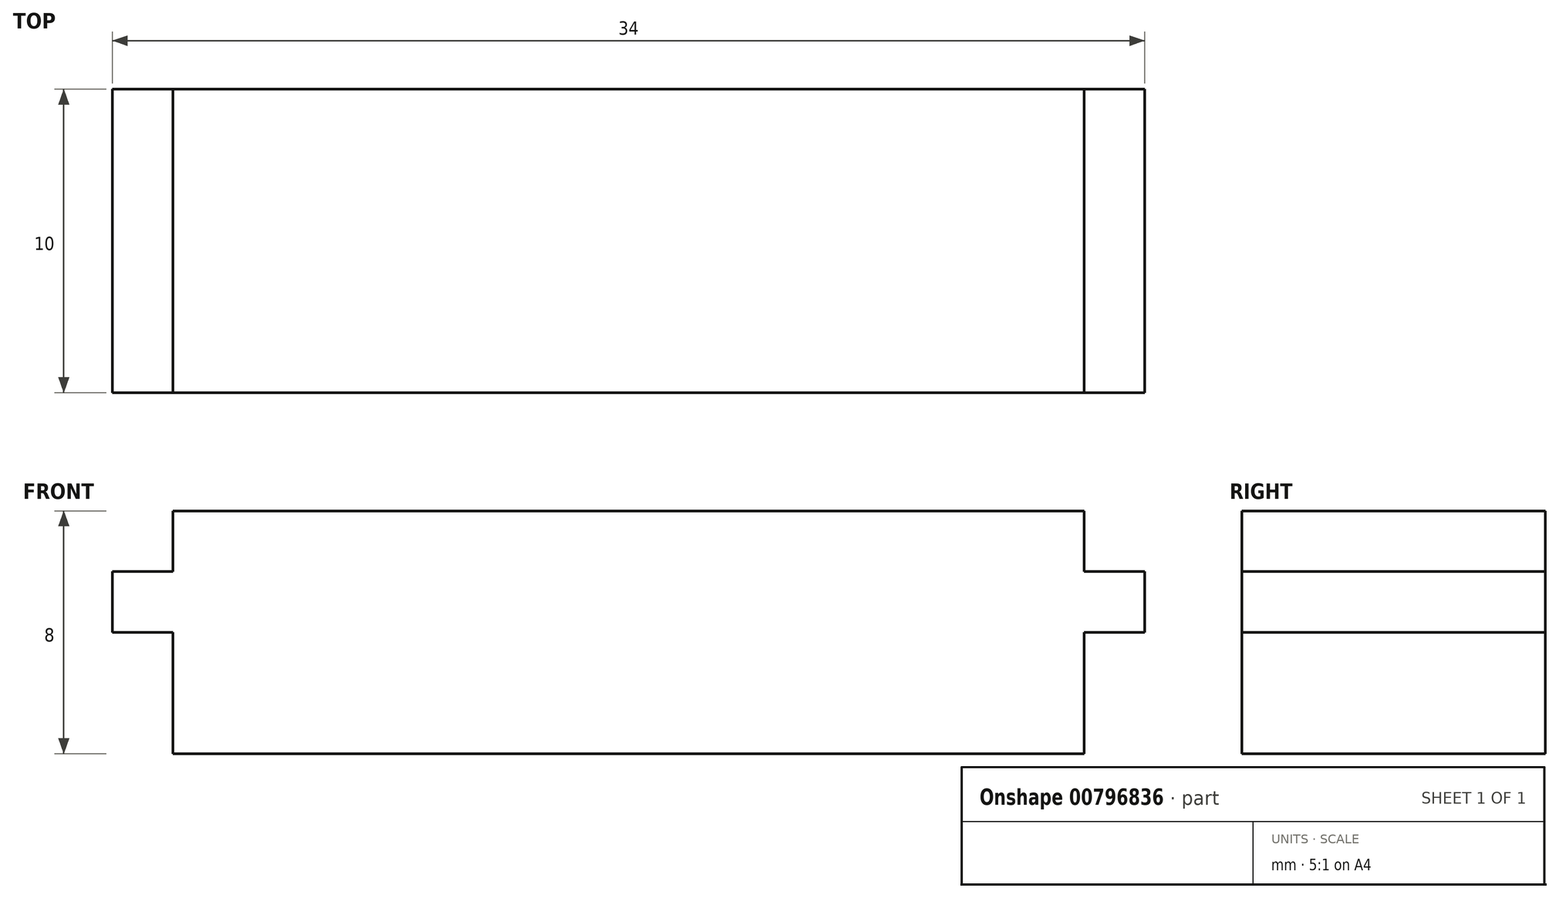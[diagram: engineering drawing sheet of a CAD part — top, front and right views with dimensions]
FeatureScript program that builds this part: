
annotation { "Feature Type Name" : "Feature", "Feature Type Description" : "" }
export const myFeature = defineFeature(function(context is Context, id is Id, definition is map)
    precondition{}
    {
        {
            var Q0;
            Q0=qCreatedBy(makeId("Top.planeOp"),FACE);
            var sketch = newSketch(context, id + "F0", { "sketchPlane" : qUnion([Q0])});
            skLineSegment(sketch, "E0.bottom", {"start": v(15, -5) * mm, "end": v(-15, -5) * mm});
            skLineSegment(sketch, "E0.top", {"start": v(15, 5) * mm, "end": v(-15, 5) * mm});
            skLineSegment(sketch, "E0.left", {"start": v(15, -5) * mm, "end": v(15, 5) * mm});
            skLineSegment(sketch, "E0.right", {"start": v(-15, -5) * mm, "end": v(-15, 5) * mm});
            skPoint(sketch, "E0.middle", {"position": v(0, 0) * mm});
            skSolve(sketch);
        }
        {
            var Q0;
            Q0=makeQuery(id+"F0.imprint","IMPRINT",FACE,{"disambiguationData":[TD([[makeQuery(id+"F0.imprint","IMPRINT",EDGE,{"derivedFrom":sQuery(id+"F0.wireOp",EDGE,"E0.bottom")}),-1.0]])]});
            extrude(context, id + "F1", {"entities" : qUnion([Q0]), "depth" : 4 * mm, "offsetDistance" : 25 * mm});
        }
        {
            var Q0;
            Q0=makeQuery(id+"F1.opExtrude","CAP_FACE",FACE,{"disambiguationData":[OSD([sQuery(id+"F0.wireOp",EDGE,"E0.bottom"),sQuery(id+"F0.wireOp",EDGE,"E0.top"),sQuery(id+"F0.wireOp",EDGE,"E0.left"),sQuery(id+"F0.wireOp",EDGE,"E0.right")])],"isStart":false});
            var sketch = newSketch(context, id + "F2", { "sketchPlane" : qUnion([Q0])});
            skLineSegment(sketch, "E1.bottom", {"start": v(17, -5) * mm, "end": v(-17, -5) * mm});
            skLineSegment(sketch, "E1.top", {"start": v(17, 5) * mm, "end": v(-17, 5) * mm});
            skLineSegment(sketch, "E1.left", {"start": v(17, -5) * mm, "end": v(17, 5) * mm});
            skLineSegment(sketch, "E1.right", {"start": v(-17, -5) * mm, "end": v(-17, 5) * mm});
            skPoint(sketch, "E1.middle", {"position": v(0, 0) * mm});
            skSolve(sketch);
        }
        {
            var Q0;
            Q0 = qSketchRegion(id + "F2", true);
            extrude(context, id + "F3", {"entities" : qUnion([Q0]), "operationType" : NewBodyOperationType.ADD, "depth" : 2 * mm, "offsetDistance" : 25 * mm});
        }
        {
            var Q0;
            Q0=makeQuery(id+"F3.opExtrude","CAP_FACE",FACE,{"disambiguationData":[OSD([sQuery(id+"F2.wireOp",EDGE,"E1.bottom"),sQuery(id+"F2.wireOp",EDGE,"E1.top"),sQuery(id+"F2.wireOp",EDGE,"E1.left"),sQuery(id+"F2.wireOp",EDGE,"E1.right")])],"isStart":false});
            var sketch = newSketch(context, id + "F4", { "sketchPlane" : qUnion([Q0])});
            skLineSegment(sketch, "E2.bottom", {"start": v(15, -5) * mm, "end": v(-15, -5) * mm});
            skLineSegment(sketch, "E2.top", {"start": v(15, 5) * mm, "end": v(-15, 5) * mm});
            skLineSegment(sketch, "E2.left", {"start": v(15, -5) * mm, "end": v(15, 5) * mm});
            skLineSegment(sketch, "E2.right", {"start": v(-15, -5) * mm, "end": v(-15, 5) * mm});
            skPoint(sketch, "E2.middle", {"position": v(0, 0) * mm});
            skSolve(sketch);
        }
        {
            var Q0;
            Q0 = qSketchRegion(id + "F4", true);
            extrude(context, id + "F5", {"entities" : qUnion([Q0]), "operationType" : NewBodyOperationType.ADD, "depth" : 1.5 * mm, "offsetDistance" : 25 * mm});
        }
        {
            var Q0;
            Q0=makeQuery(id+"F5.opExtrude","CAP_FACE",FACE,{"disambiguationData":[OSD([sQuery(id+"F4.wireOp",EDGE,"E2.bottom"),sQuery(id+"F4.wireOp",EDGE,"E2.top"),sQuery(id+"F4.wireOp",EDGE,"E2.left"),sQuery(id+"F4.wireOp",EDGE,"E2.right")])],"isStart":false});
            var sketch = newSketch(context, id + "F6", { "sketchPlane" : qUnion([Q0])});
            skLineSegment(sketch, "E3.bottom", {"start": v(15, -5) * mm, "end": v(-15, -5) * mm});
            skLineSegment(sketch, "E3.top", {"start": v(15, 5) * mm, "end": v(-15, 5) * mm});
            skLineSegment(sketch, "E3.left", {"start": v(15, -5) * mm, "end": v(15, 5) * mm});
            skLineSegment(sketch, "E3.right", {"start": v(-15, -5) * mm, "end": v(-15, 5) * mm});
            skPoint(sketch, "E3.middle", {"position": v(0, 0) * mm});
            skSolve(sketch);
        }
        {
            var Q0;
            Q0 = qSketchRegion(id + "F6", true);
            extrude(context, id + "F7", {"entities" : qUnion([Q0]), "operationType" : NewBodyOperationType.ADD, "depth" : .5 * mm, "offsetDistance" : 25 * mm});
        }
    });
